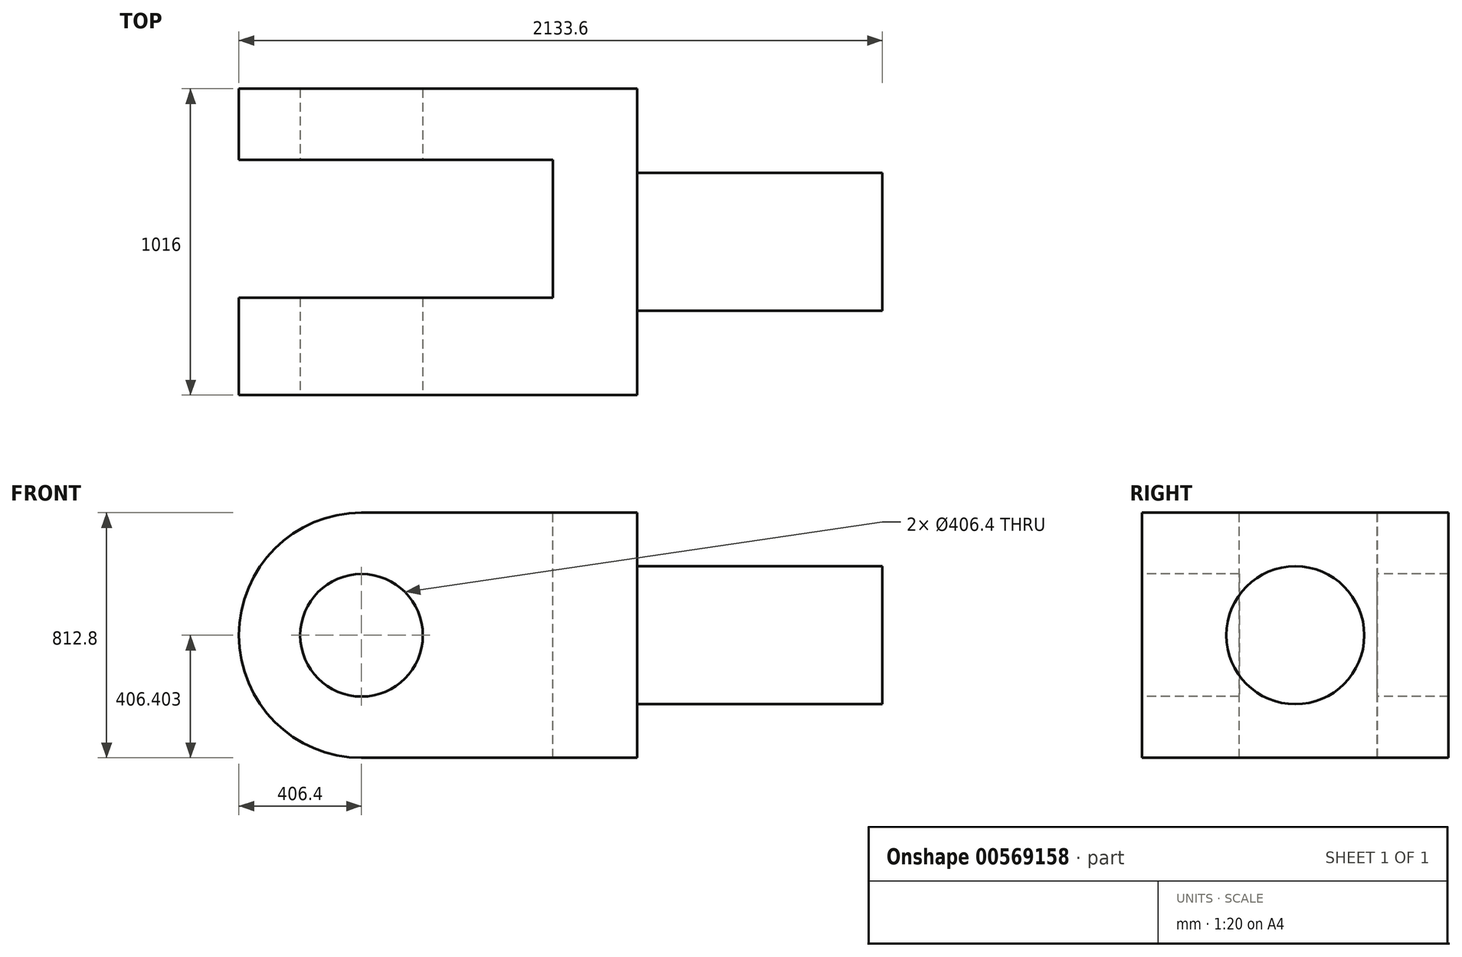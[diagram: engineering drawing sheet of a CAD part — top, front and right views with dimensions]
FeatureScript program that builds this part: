
annotation { "Feature Type Name" : "Feature", "Feature Type Description" : "" }
export const myFeature = defineFeature(function(context is Context, id is Id, definition is map)
    precondition{}
    {
        {
            var Q0;
            Q0=qCreatedBy(makeId("Front.planeOp"),FACE);
            var sketch = newSketch(context, id + "F0", { "sketchPlane" : qUnion([Q0])});
            skLineSegment(sketch, "E0", {"start": v(0, 70.9) * mm, "end": v(914.4, 70.9) * mm});
            skLineSegment(sketch, "E1", {"start": v(914.4, 70.9) * mm, "end": v(914.4, -741.9) * mm});
            skLineSegment(sketch, "E2", {"start": v(914.4, -741.9) * mm, "end": v(0, -741.9) * mm});
            skLineSegment(sketch, "E3", {"start": v(0, -741.9) * mm, "end": v(0, 70.9) * mm});
            skCircle(sketch, "E4", {"center": v(0, -335.5) * mm, "radius": 203.2 * mm});
            skLineSegment(sketch, "E5", {"start": v(0, -741.9) * mm, "end": v(0, -741.9) * mm});
            skLineSegment(sketch, "E6", {"start": v(-406.4, -335.5) * mm, "end": v(-406.4, -335.5) * mm});
            skLineSegment(sketch, "E7", {"start": v(0, 70.9) * mm, "end": v(0, 70.9) * mm});
            skPoint(sketch, "E8.visualSharp", {"position": v(-406.4, -741.9) * mm});
            skArc(sketch, "E8.filletArc", {"start": v(-406.4, -335.5) * mm, "mid": v(-287.37, -622.88) * mm, "end": v(0, -741.9) * mm});
            skPoint(sketch, "E9.visualSharp", {"position": v(-406.4, 70.9) * mm});
            skArc(sketch, "E9.filletArc", {"start": v(0, 70.9) * mm, "mid": v(-287.37, -48.14) * mm, "end": v(-406.4, -335.5) * mm});
            skSolve(sketch);
        }
        {
            var Q0;
            {var subQ4=sQuery(id+"F0.wireOp",EDGE,"E0");Q0=makeQuery(id+"F0.imprint","IMPRINT",FACE,{"disambiguationData":[TD([[makeQuery(id+"F0.imprint","IMPRINT",EDGE,{"derivedFrom":subQ4}),-1.0]])]});}
            var Q1;
            {var subQ5=sQuery(id+"F0.wireOp",EDGE,"E8.filletArc");Q1=makeQuery(id+"F0.imprint","IMPRINT",FACE,{"disambiguationData":[TD([[makeQuery(id+"F0.imprint","IMPRINT",EDGE,{"derivedFrom":subQ5}),1.0]])]});}
            extrude(context, id + "F1", {"entities" : qUnion([Q0, Q1]), "oppositeDirection" : true, "depth" : 1016 * mm, "offsetDistance" : 25.4 * mm});
        }
        {
            var Q0;
            Q0=makeQuery(id+"F1.opExtrude","SWEPT_FACE",FACE,{"disambiguationData":[OSD([sQuery(id+"F0.wireOp",EDGE,"E0")])]});
            var sketch = newSketch(context, id + "F2", { "sketchPlane" : qUnion([Q0])});
            skLineSegment(sketch, "E10", {"start": v(0, 779.64) * mm, "end": v(635, 779.64) * mm});
            skLineSegment(sketch, "E11", {"start": v(635, 779.64) * mm, "end": v(635, 322.44) * mm});
            skLineSegment(sketch, "E12", {"start": v(635, 322.44) * mm, "end": v(0, 322.44) * mm});
            skLineSegment(sketch, "E13", {"start": v(0, 322.44) * mm, "end": v(-406.4, 322.44) * mm});
            skLineSegment(sketch, "E14", {"start": v(-406.4, 322.44) * mm, "end": v(-406.4, 779.64) * mm});
            skLineSegment(sketch, "E15", {"start": v(-406.4, 779.64) * mm, "end": v(0, 779.64) * mm});
            skSolve(sketch);
        }
        {
            var Q0;
            {var subQ0=sQuery(id+"F2.wireOp",EDGE,"E13");Q0=makeQuery(id+"F2.imprint","IMPRINT",FACE,{"disambiguationData":[TD([[makeQuery(id+"F2.imprint","IMPRINT",EDGE,{"derivedFrom":subQ0}),-1.0]])]});}
            var Q1;
            {var subQ0=sQuery(id+"F2.wireOp",EDGE,"E10");Q1=makeQuery(id+"F2.imprint","IMPRINT",FACE,{"disambiguationData":[TD([[makeQuery(id+"F2.imprint","IMPRINT",EDGE,{"derivedFrom":subQ0}),-1.0]])]});}
            extrude(context, id + "F3", {"entities" : qUnion([Q0, Q1]), "operationType" : NewBodyOperationType.REMOVE, "endBound" : BoundingType.THROUGH_ALL, "oppositeDirection" : true, "depth" : 25.4 * mm, "offsetDistance" : 25.4 * mm});
        }
        {
            var Q0;
            Q0=makeQuery(id+"F1.opExtrude","SWEPT_FACE",FACE,{"disambiguationData":[OSD([sQuery(id+"F0.wireOp",EDGE,"E1")])]});
            var sketch = newSketch(context, id + "F4", { "sketchPlane" : qUnion([Q0])});
            skCircle(sketch, "E16", {"center": v(508, -335.5) * mm, "radius": 228.6 * mm});
            skSolve(sketch);
        }
        {
            var Q0;
            Q0=makeQuery(id+"F4.imprint","IMPRINT",FACE,{"disambiguationData":[TD([[makeQuery(id+"F4.imprint","IMPRINT",EDGE,{"derivedFrom":sQuery(id+"F4.wireOp",EDGE,"E16")}),1.0]])]});
            extrude(context, id + "F5", {"entities" : qUnion([Q0]), "operationType" : NewBodyOperationType.ADD, "depth" : 812.8 * mm, "offsetDistance" : 25.4 * mm});
        }
    });
